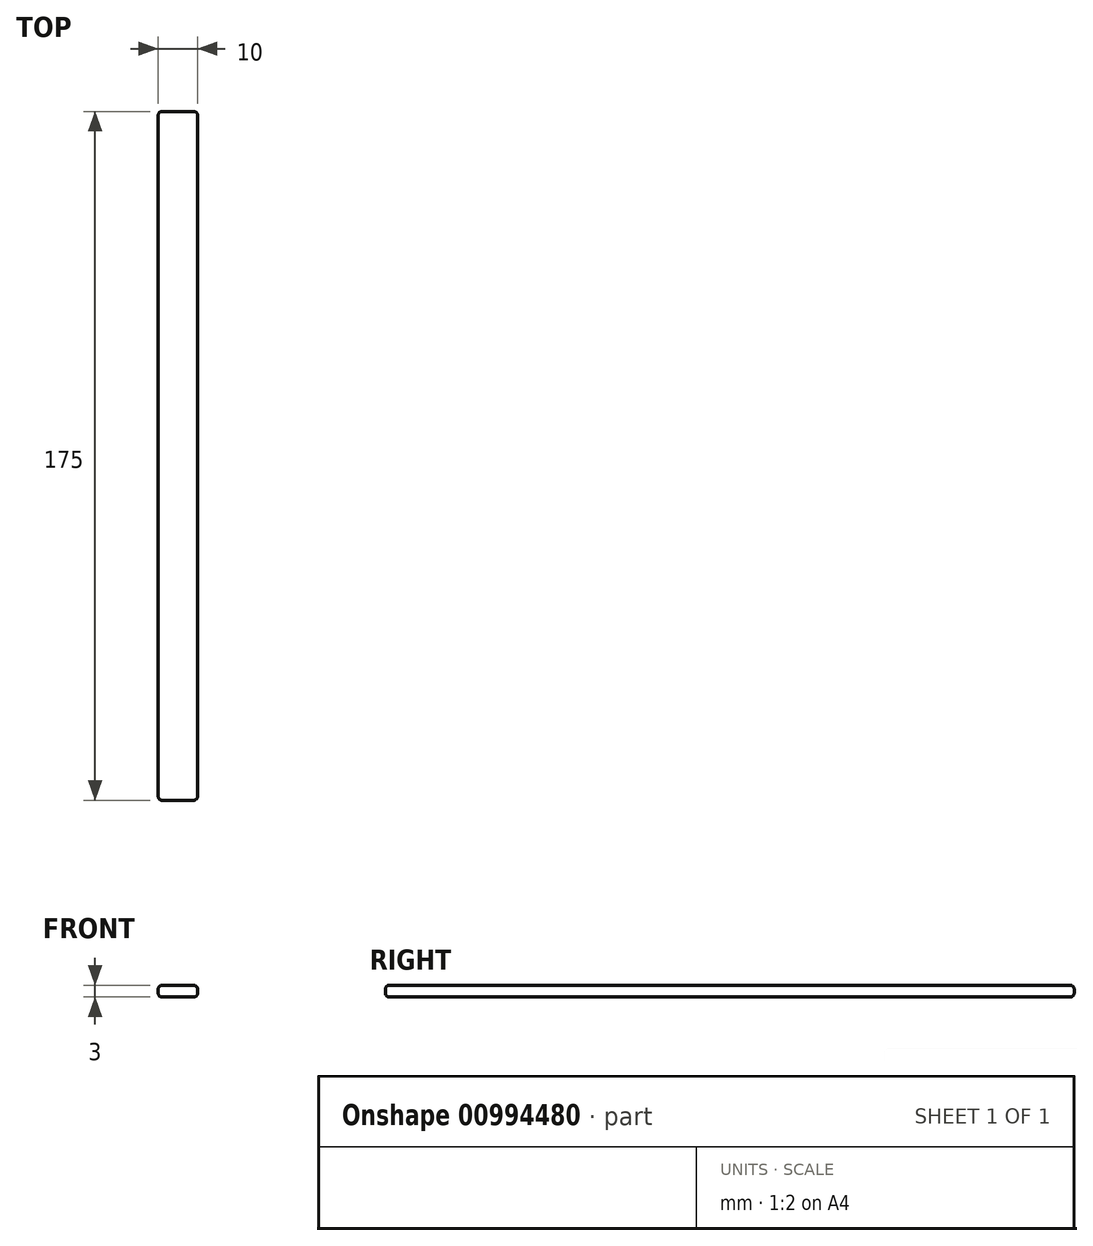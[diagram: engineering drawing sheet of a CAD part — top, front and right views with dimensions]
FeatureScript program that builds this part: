
annotation { "Feature Type Name" : "Feature", "Feature Type Description" : "" }
export const myFeature = defineFeature(function(context is Context, id is Id, definition is map)
    precondition{}
    {
        {
            assignVariable(context, id + "F0", {"name" : "reinforcer_length", "anyValue" : 175});
        }
        {
            var Q0;
            Q0=qCreatedBy(makeId("Front.planeOp"),FACE);
            var sketch = newSketch(context, id + "F1", { "sketchPlane" : qUnion([Q0])});
            skLineSegment(sketch, "E0.bottom", {"start": v(5, 0) * mm, "end": v(-5, 0) * mm});
            skLineSegment(sketch, "E0.top", {"start": v(5, 3) * mm, "end": v(-5, 3) * mm});
            skLineSegment(sketch, "E0.left", {"start": v(5, 0) * mm, "end": v(5, 3) * mm});
            skLineSegment(sketch, "E0.right", {"start": v(-5, 0) * mm, "end": v(-5, 3) * mm});
            skSolve(sketch);
        }
        {
            var Q0;
            Q0=makeQuery(id+"F1.imprint","IMPRINT",FACE,{"disambiguationData":[TD([[makeQuery(id+"F1.imprint","IMPRINT",EDGE,{"derivedFrom":sQuery(id+"F1.wireOp",EDGE,"E0.bottom")}),-1.0]])]});
            extrude(context, id + "F2", {"entities" : qUnion([Q0]), "depth" : (getVariable(context, 'reinforcer_length')) * mm, "offsetDistance" : 25 * mm, "symmetric" : true});
        }
        {
            var Q0;
            Q0=makeQuery(id+"F2.opExtrude","CAP_EDGE",EDGE,{"disambiguationData":[OSD([sQuery(id+"F1.wireOp",EDGE,"E0.top")])],"isStart":false});
            var Q1;
            Q1=makeQuery(id+"F2.opExtrude","CAP_EDGE",EDGE,{"disambiguationData":[OSD([sQuery(id+"F1.wireOp",EDGE,"E0.left")])],"isStart":false});
            var Q2;
            Q2=makeQuery(id+"F2.opExtrude","CAP_EDGE",EDGE,{"disambiguationData":[OSD([sQuery(id+"F1.wireOp",EDGE,"E0.bottom")])],"isStart":false});
            var Q3;
            Q3=makeQuery(id+"F2.opExtrude","CAP_EDGE",EDGE,{"disambiguationData":[OSD([sQuery(id+"F1.wireOp",EDGE,"E0.right")])],"isStart":false});
            var Q4;
            Q4=makeQuery(id+"F2.opExtrude","SWEPT_EDGE",EDGE,{"disambiguationData":[OSD([sQuery(id+"F1.wireOp",EDGE,"E0.top"),sQuery(id+"F1.wireOp",EDGE,"E0.right")])]});
            var Q5;
            Q5=makeQuery(id+"F2.opExtrude","SWEPT_EDGE",EDGE,{"disambiguationData":[OSD([sQuery(id+"F1.wireOp",EDGE,"E0.top"),sQuery(id+"F1.wireOp",EDGE,"E0.left")])]});
            var Q6;
            Q6=makeQuery(id+"F2.opExtrude","SWEPT_EDGE",EDGE,{"disambiguationData":[OSD([sQuery(id+"F1.wireOp",EDGE,"E0.bottom"),sQuery(id+"F1.wireOp",EDGE,"E0.left")])]});
            var Q7;
            Q7=makeQuery(id+"F2.opExtrude","SWEPT_EDGE",EDGE,{"disambiguationData":[OSD([sQuery(id+"F1.wireOp",EDGE,"E0.bottom"),sQuery(id+"F1.wireOp",EDGE,"E0.right")])]});
            var Q8;
            Q8=makeQuery(id+"F2.opExtrude","CAP_EDGE",EDGE,{"disambiguationData":[OSD([sQuery(id+"F1.wireOp",EDGE,"E0.bottom")])],"isStart":true});
            var Q9;
            Q9=makeQuery(id+"F2.opExtrude","CAP_EDGE",EDGE,{"disambiguationData":[OSD([sQuery(id+"F1.wireOp",EDGE,"E0.left")])],"isStart":true});
            var Q10;
            Q10=makeQuery(id+"F2.opExtrude","CAP_EDGE",EDGE,{"disambiguationData":[OSD([sQuery(id+"F1.wireOp",EDGE,"E0.top")])],"isStart":true});
            var Q11;
            Q11=makeQuery(id+"F2.opExtrude","CAP_EDGE",EDGE,{"disambiguationData":[OSD([sQuery(id+"F1.wireOp",EDGE,"E0.right")])],"isStart":true});
            fillet(context, id + "F3", {"entities" : qUnion([Q0, Q1, Q2, Q3, Q4, Q5, Q6, Q7, Q8, Q9, Q10, Q11]), "radius" : 1 * mm, "tangentPropagation" : true, "allowEdgeOverflow" : false});
        }
    });
